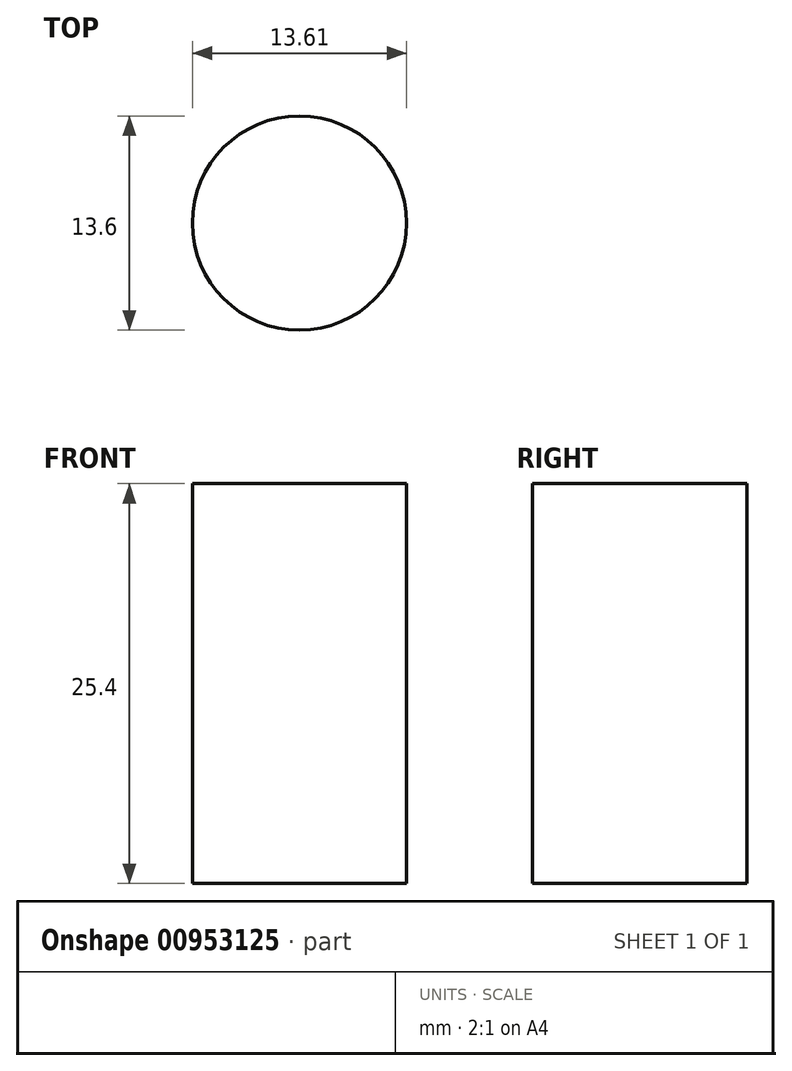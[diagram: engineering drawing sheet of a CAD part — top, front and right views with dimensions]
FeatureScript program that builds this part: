
annotation { "Feature Type Name" : "Feature", "Feature Type Description" : "" }
export const myFeature = defineFeature(function(context is Context, id is Id, definition is map)
    precondition{}
    {
        {
            var Q0;
            Q0=qCreatedBy(makeId("Top.planeOp"),FACE);
            var sketch = newSketch(context, id + "F0", { "sketchPlane" : qUnion([Q0])});
            skCircle(sketch, "E0", {"center": v(-37.93, 32.45) * mm, "radius": 6.8 * mm});
            skSolve(sketch);
        }
        {
            var Q0;
            Q0=makeQuery(id+"F0.imprint","IMPRINT",FACE,{"disambiguationData":[TD([[makeQuery(id+"F0.imprint","IMPRINT",EDGE,{"derivedFrom":sQuery(id+"F0.wireOp",EDGE,"E0")}),1.0]])]});
            extrude(context, id + "F1", {"entities" : qUnion([Q0]), "depth" : 25.4 * mm, "offsetDistance" : 25.4 * mm});
        }
    });
